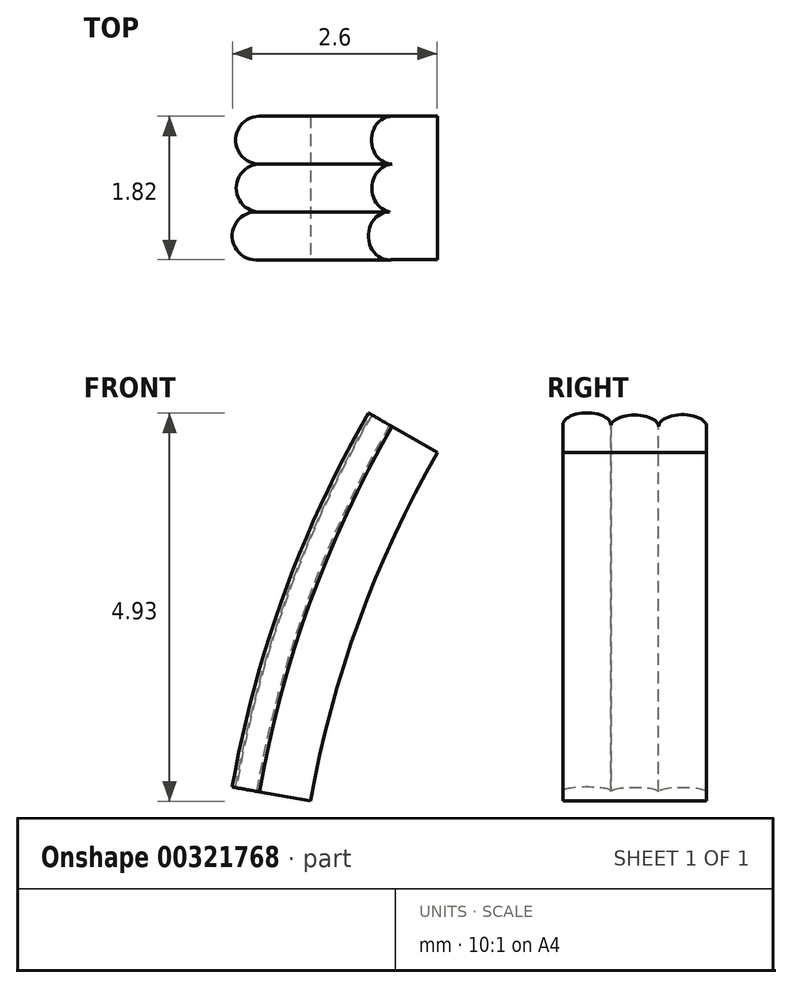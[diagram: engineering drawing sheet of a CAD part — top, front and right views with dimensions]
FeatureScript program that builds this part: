
annotation { "Feature Type Name" : "Feature", "Feature Type Description" : "" }
export const myFeature = defineFeature(function(context is Context, id is Id, definition is map)
    precondition{}
    {
        {
            var Q0;
            Q0=qCreatedBy(makeId("Top.planeOp"),FACE);
            var sketch = newSketch(context, id + "F0", { "sketchPlane" : qUnion([Q0])});
            skLineSegment(sketch, "E0.bottom", {"start": v(-14.22, -12.1) * mm, "end": v(-13.55, -12.1) * mm});
            skLineSegment(sketch, "E0.top", {"start": v(-14.22, -13.93) * mm, "end": v(-13.55, -13.93) * mm});
            skLineSegment(sketch, "E0.right", {"start": v(-13.55, -12.1) * mm, "end": v(-13.55, -13.93) * mm});
            skLineSegment(sketch, "E1", {"start": v(0, 0) * mm, "end": v(0, -13.55) * mm});
            skArc(sketch, "E2", {"start": v(-14.22, -12.1) * mm, "mid": v(-14.52, -12.41) * mm, "end": v(-14.22, -12.72) * mm});
            skArc(sketch, "E3", {"start": v(-14.22, -12.72) * mm, "mid": v(-14.51, -13.02) * mm, "end": v(-14.22, -13.33) * mm});
            skArc(sketch, "E4", {"start": v(-14.22, -13.33) * mm, "mid": v(-14.57, -13.63) * mm, "end": v(-14.22, -13.93) * mm});
            skSolve(sketch);
        }
        {
            var Q0;
            Q0 = qSketchRegion(id + "F0", true);
            var Q1;
            Q1=sQuery(id+"F0.wireOp",EDGE,"E1");
            revolve(context, id + "F1", {"entities" : qUnion([Q0]), "axis" : qUnion([Q1]), "revolveType" : RevolveType.TWO_DIRECTIONS, "angle" : 350 * degree, "angleBack" : 330 * degree});
        }
    });
